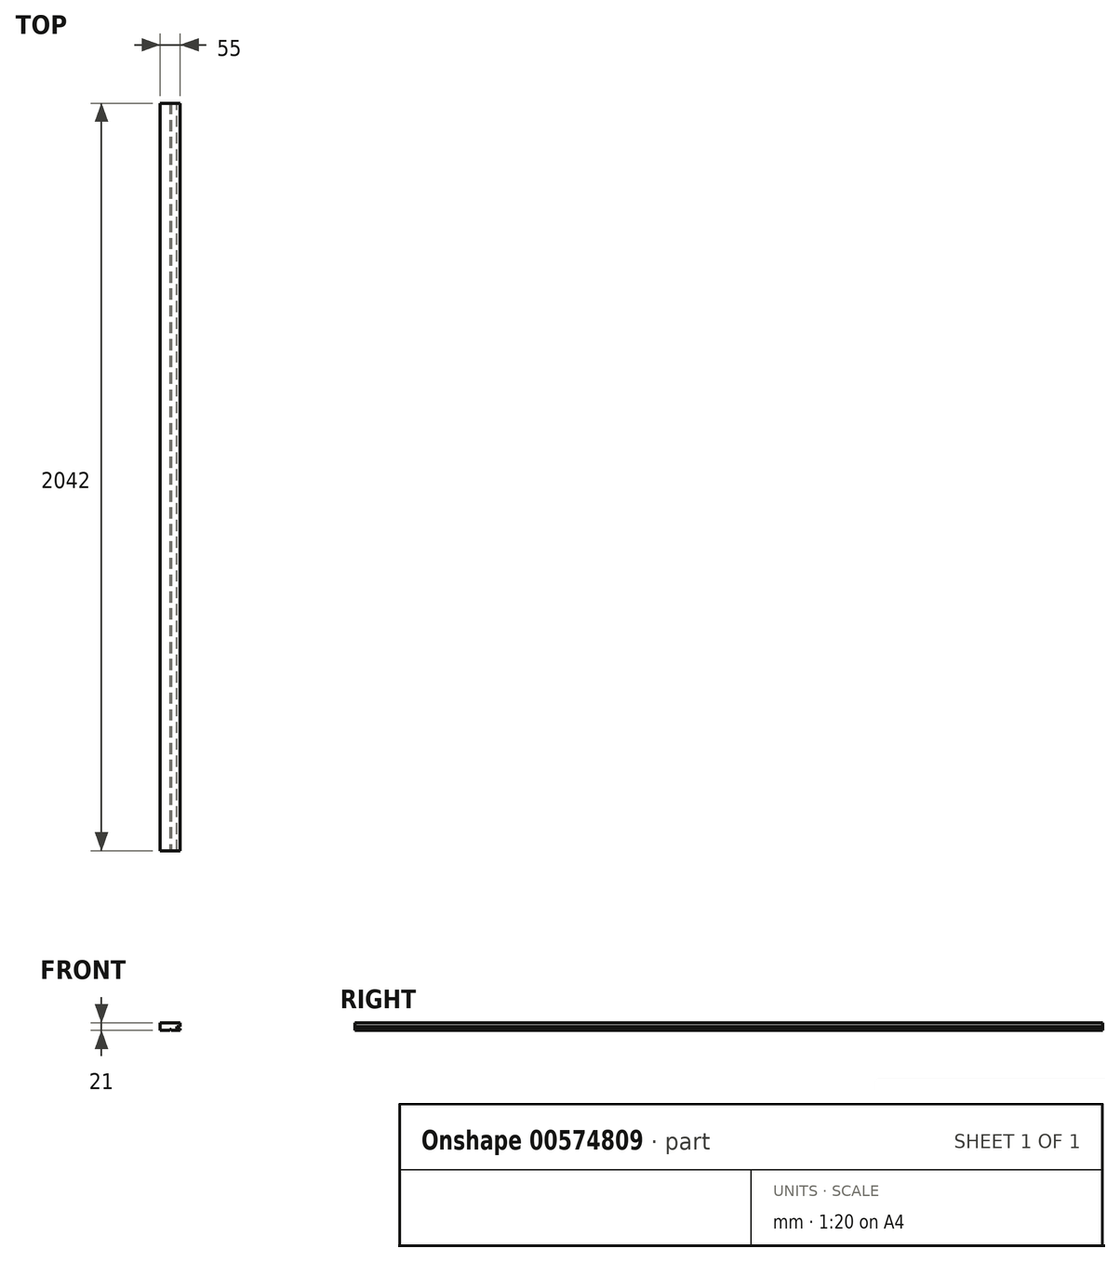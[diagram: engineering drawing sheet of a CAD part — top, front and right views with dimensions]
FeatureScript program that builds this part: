
annotation { "Feature Type Name" : "Feature", "Feature Type Description" : "" }
export const myFeature = defineFeature(function(context is Context, id is Id, definition is map)
    precondition{}
    {
        {
            var Q0;
            Q0=qCreatedBy(makeId("Front.planeOp"),FACE);
            var sketch = newSketch(context, id + "F0", { "sketchPlane" : qUnion([Q0])});
            skLineSegment(sketch, "E0", {"start": v(-21.73, 10.5) * mm, "end": v(47.5, 10.5) * mm});
            skLineSegment(sketch, "E1", {"start": v(47.5, 10.5) * mm, "end": v(47.5, 0.5) * mm});
            skLineSegment(sketch, "E2", {"start": v(47.5, 0.5) * mm, "end": v(37.5, 0.5) * mm});
            skLineSegment(sketch, "E3", {"start": v(37.5, 0.5) * mm, "end": v(37.5, -4.5) * mm});
            skLineSegment(sketch, "E4", {"start": v(37.5, -4.5) * mm, "end": v(47.5, -4.5) * mm});
            skLineSegment(sketch, "E5", {"start": v(47.5, -4.5) * mm, "end": v(47.5, -10.5) * mm});
            skLineSegment(sketch, "E6", {"start": v(47.5, -10.5) * mm, "end": v(-37.5, -10.5) * mm});
            skLineSegment(sketch, "E7", {"start": v(-37.5, -10.5) * mm, "end": v(-37.5, -4.5) * mm});
            skLineSegment(sketch, "E8", {"start": v(-37.5, -4.5) * mm, "end": v(-47.5, -4.5) * mm});
            skLineSegment(sketch, "E9", {"start": v(-47.5, -4.5) * mm, "end": v(-47.5, 0.5) * mm});
            skLineSegment(sketch, "E10", {"start": v(-47.5, 0.5) * mm, "end": v(-27.5, 0.5) * mm});
            skLineSegment(sketch, "E11", {"start": v(-27.5, 0.5) * mm, "end": v(-21.73, 10.5) * mm});
            skSolve(sketch);
        }
        {
            var Q0;
            Q0=qSketchRegion(id+"F0",true);
            extrude(context, id + "F1", {"entities" : qUnion([Q0]), "depth" : 2042 * mm, "offsetDistance" : 25 * mm});
        }
        {
            var Q0;
            Q0=makeQuery(id+"F1.opExtrude","CAP_FACE",FACE,{"disambiguationData":[OSD([sQuery(id+"F0.wireOp",EDGE,"E0"),sQuery(id+"F0.wireOp",EDGE,"E1"),sQuery(id+"F0.wireOp",EDGE,"E2"),sQuery(id+"F0.wireOp",EDGE,"E3"),sQuery(id+"F0.wireOp",EDGE,"E4"),sQuery(id+"F0.wireOp",EDGE,"E5"),sQuery(id+"F0.wireOp",EDGE,"E6"),sQuery(id+"F0.wireOp",EDGE,"E7"),sQuery(id+"F0.wireOp",EDGE,"E8"),sQuery(id+"F0.wireOp",EDGE,"E9"),sQuery(id+"F0.wireOp",EDGE,"E10"),sQuery(id+"F0.wireOp",EDGE,"E11")])],"isStart":false});
            var sketch = newSketch(context, id + "F2", { "sketchPlane" : qUnion([Q0])});
            skLineSegment(sketch, "E12.bottom", {"start": v(19.5, -10.5) * mm, "end": v(22.5, -10.5) * mm});
            skLineSegment(sketch, "E12.top", {"start": v(19.5, -7.5) * mm, "end": v(22.5, -7.5) * mm});
            skLineSegment(sketch, "E12.left", {"start": v(19.5, -10.5) * mm, "end": v(19.5, -7.5) * mm});
            skLineSegment(sketch, "E12.right", {"start": v(22.5, -10.5) * mm, "end": v(22.5, -7.5) * mm});
            skLineSegment(sketch, "E13.bottom", {"start": v(-7.5, -10.5) * mm, "end": v(-47.5, -10.5) * mm});
            skLineSegment(sketch, "E13.top", {"start": v(-7.5, 10.5) * mm, "end": v(-47.5, 10.5) * mm});
            skLineSegment(sketch, "E13.left", {"start": v(-7.5, -10.5) * mm, "end": v(-7.5, 10.5) * mm});
            skLineSegment(sketch, "E13.right", {"start": v(-47.5, -10.5) * mm, "end": v(-47.5, 10.5) * mm});
            skSolve(sketch);
        }
        {
            var Q0;
            Q0 = qSketchRegion(id + "F2", true);
            extrude(context, id + "F3", {"entities" : qUnion([Q0]), "operationType" : NewBodyOperationType.REMOVE, "endBound" : BoundingType.THROUGH_ALL, "oppositeDirection" : true, "depth" : 25 * mm, "offsetDistance" : 25 * mm});
        }
    });
